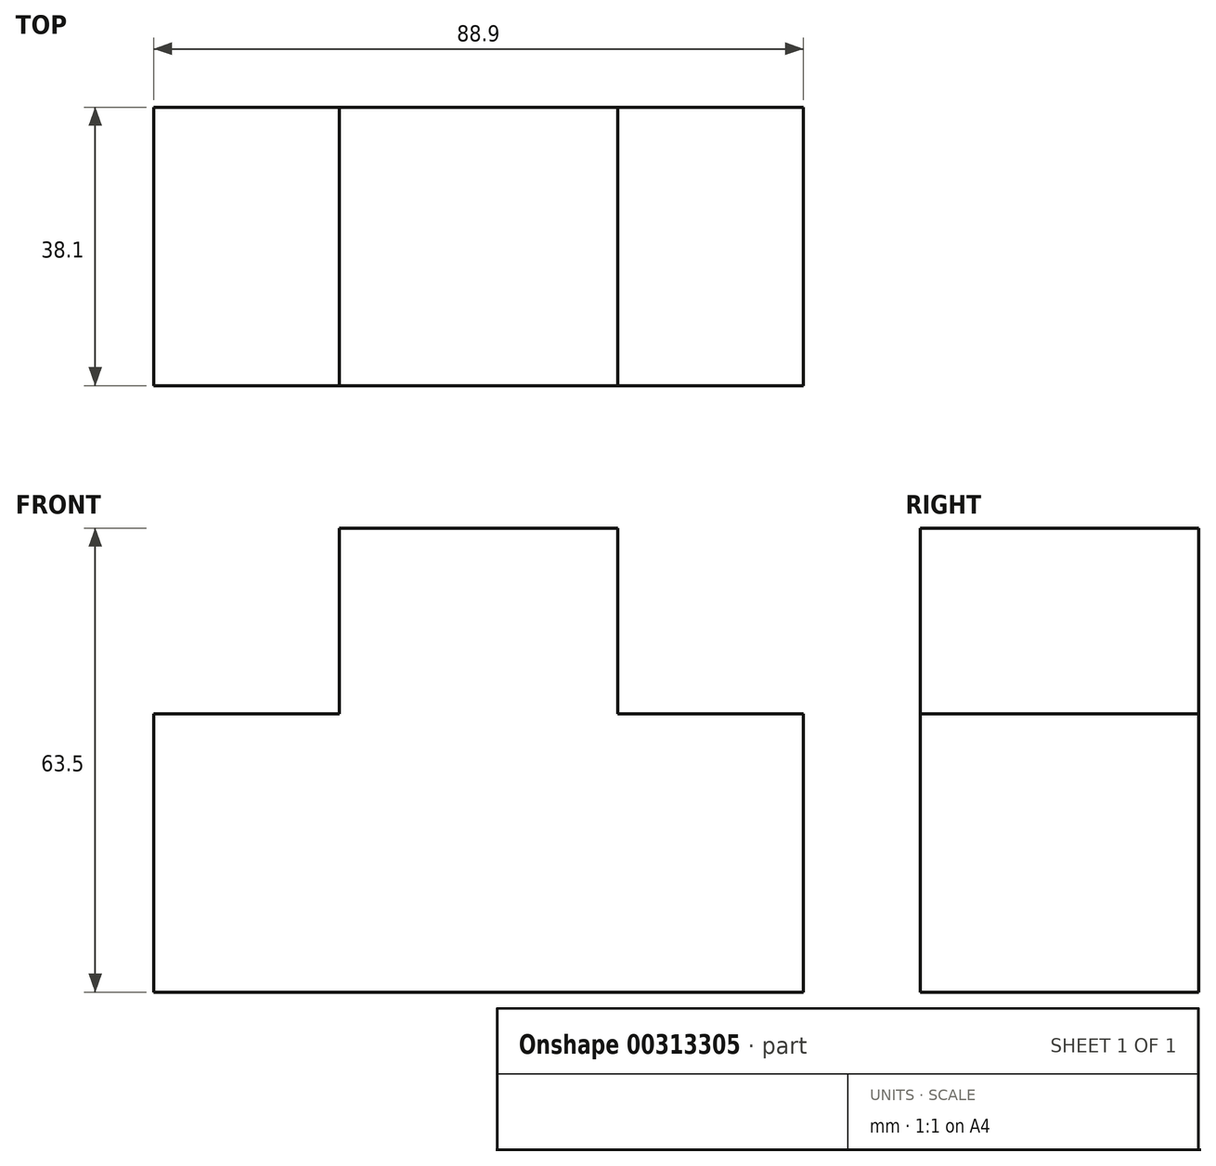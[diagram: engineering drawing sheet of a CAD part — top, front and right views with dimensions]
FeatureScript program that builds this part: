
annotation { "Feature Type Name" : "Feature", "Feature Type Description" : "" }
export const myFeature = defineFeature(function(context is Context, id is Id, definition is map)
    precondition{}
    {
        {
            var Q0;
            Q0=qCreatedBy(makeId("Front.planeOp"),FACE);
            var sketch = newSketch(context, id + "F0", { "sketchPlane" : qUnion([Q0])});
            skLineSegment(sketch, "E0", {"start": v(-52.72, -42.87) * mm, "end": v(36.18, -42.87) * mm});
            skLineSegment(sketch, "E1", {"start": v(36.18, -42.87) * mm, "end": v(36.18, -4.77) * mm});
            skLineSegment(sketch, "E2", {"start": v(36.18, -4.77) * mm, "end": v(10.78, -4.77) * mm});
            skLineSegment(sketch, "E3", {"start": v(10.78, -4.77) * mm, "end": v(10.78, 20.63) * mm});
            skLineSegment(sketch, "E4", {"start": v(10.78, 20.63) * mm, "end": v(-27.32, 20.63) * mm});
            skLineSegment(sketch, "E5", {"start": v(-27.32, 20.63) * mm, "end": v(-27.32, -4.77) * mm});
            skLineSegment(sketch, "E6", {"start": v(-27.32, -4.77) * mm, "end": v(-52.72, -4.77) * mm});
            skLineSegment(sketch, "E7", {"start": v(-52.72, -4.77) * mm, "end": v(-52.72, -42.87) * mm});
            skSolve(sketch);
        }
        {
            var Q0;
            Q0 = qSketchRegion(id + "F0", true);
            extrude(context, id + "F1", {"entities" : qUnion([Q0]), "depth" : 38.1 * mm});
        }
    });
